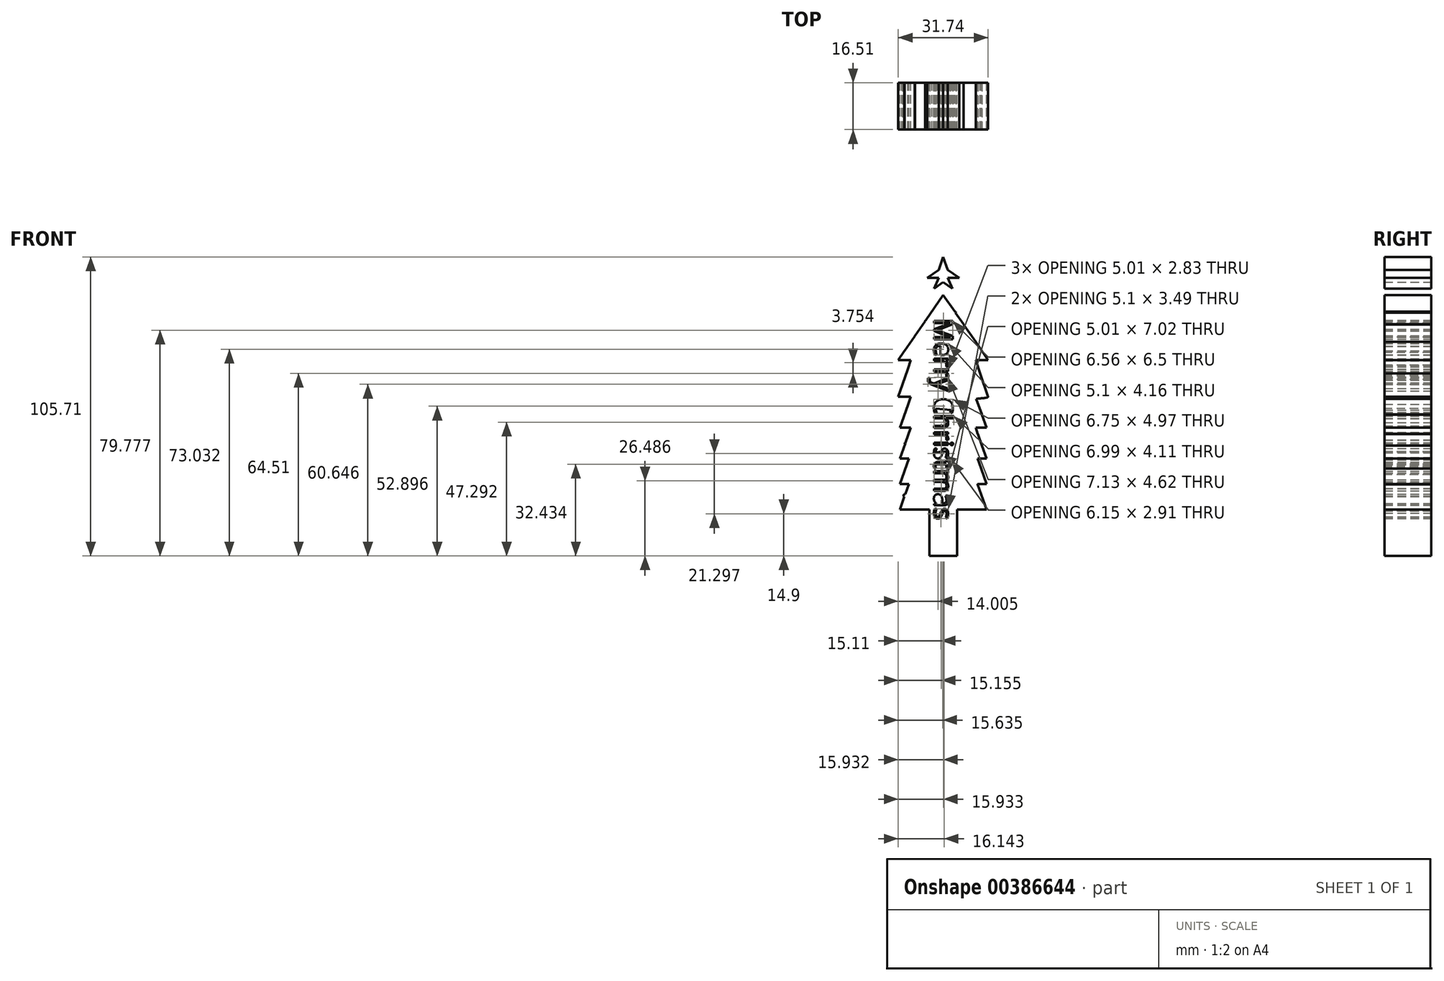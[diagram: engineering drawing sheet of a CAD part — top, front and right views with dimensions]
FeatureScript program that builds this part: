
annotation { "Feature Type Name" : "Feature", "Feature Type Description" : "" }
export const myFeature = defineFeature(function(context is Context, id is Id, definition is map)
    precondition{}
    {
        {
            var Q0;
            Q0=qCreatedBy(makeId("Front.planeOp"),FACE);
            var sketch = newSketch(context, id + "F0", { "sketchPlane" : qUnion([Q0])});
            skLineSegment(sketch, "E0", {"start": v(0, -45.28) * mm, "end": v(-4.85, -45.28) * mm});
            skLineSegment(sketch, "E1", {"start": v(-4.85, -45.28) * mm, "end": v(-4.85, -28.85) * mm});
            skLineSegment(sketch, "E2", {"start": v(-4.85, -28.85) * mm, "end": v(-15.31, -28.85) * mm});
            skLineSegment(sketch, "E3", {"start": v(-15.31, -28.85) * mm, "end": v(-12.14, -19.89) * mm});
            skLineSegment(sketch, "E4", {"start": v(-12.14, -19.89) * mm, "end": v(-15.31, -19.89) * mm});
            skLineSegment(sketch, "E5", {"start": v(-15.31, -19.89) * mm, "end": v(-12.14, -10.92) * mm});
            skLineSegment(sketch, "E6", {"start": v(-12.14, -10.92) * mm, "end": v(-15.31, -10.92) * mm});
            skLineSegment(sketch, "E7", {"start": v(-15.31, -10.92) * mm, "end": v(-11.44, 0) * mm});
            skLineSegment(sketch, "E8", {"start": v(-11.44, 0) * mm, "end": v(-15.31, 0) * mm});
            skLineSegment(sketch, "E9", {"start": v(-15.31, 0) * mm, "end": v(-11.44, 10.92) * mm});
            skLineSegment(sketch, "E10", {"start": v(-11.44, 10.92) * mm, "end": v(-15.87, 10.92) * mm});
            skLineSegment(sketch, "E11", {"start": v(-15.87, 10.92) * mm, "end": v(-11.44, 24) * mm});
            skLineSegment(sketch, "E12", {"start": v(-11.44, 24) * mm, "end": v(-15.87, 24) * mm});
            skLineSegment(sketch, "E13", {"start": v(-15.87, 24) * mm, "end": v(0, 46.96) * mm});
            skLineSegment(sketch, "E14", {"start": v(0, 46.96) * mm, "end": v(0, -45.28) * mm, "construction": true});
            skLineSegment(sketch, "E15.MirrorCS", {"start": v(15.87, 24) * mm, "end": v(0, 46.96) * mm});
            skLineSegment(sketch, "E16.MirrorCS", {"start": v(15.87, 10.92) * mm, "end": v(11.44, 24) * mm});
            skLineSegment(sketch, "E17.MirrorCS", {"start": v(11.44, 24) * mm, "end": v(15.87, 24) * mm});
            skLineSegment(sketch, "E18.MirrorCS", {"start": v(11.44, 10.92) * mm, "end": v(15.87, 10.92) * mm});
            skLineSegment(sketch, "E19.MirrorCS", {"start": v(15.31, 0) * mm, "end": v(11.44, 10.92) * mm});
            skLineSegment(sketch, "E20.MirrorCS", {"start": v(11.44, 0) * mm, "end": v(15.31, 0) * mm});
            skLineSegment(sketch, "E21.MirrorCS", {"start": v(15.31, -10.92) * mm, "end": v(11.44, 0) * mm});
            skLineSegment(sketch, "E22.MirrorCS", {"start": v(12.14, -10.92) * mm, "end": v(15.31, -10.92) * mm});
            skLineSegment(sketch, "E23.MirrorCS", {"start": v(15.31, -19.89) * mm, "end": v(12.14, -10.92) * mm});
            skLineSegment(sketch, "E24.MirrorCS", {"start": v(12.14, -19.89) * mm, "end": v(15.31, -19.89) * mm});
            skLineSegment(sketch, "E25.MirrorCS", {"start": v(15.31, -28.85) * mm, "end": v(12.14, -19.89) * mm});
            skLineSegment(sketch, "E26.MirrorCS", {"start": v(4.85, -28.85) * mm, "end": v(15.31, -28.85) * mm});
            skLineSegment(sketch, "E27.MirrorCS", {"start": v(4.85, -45.28) * mm, "end": v(4.85, -28.85) * mm});
            skLineSegment(sketch, "E28.MirrorCS", {"start": v(0, -45.28) * mm, "end": v(4.85, -45.28) * mm});
            skLineSegment(sketch, "E29", {"start": v(0, 51.48) * mm, "end": v(0, 46.96) * mm});
            skLineSegment(sketch, "E30", {"start": v(0, 51.48) * mm, "end": v(-3.26, 49.22) * mm});
            skPoint(sketch, "E30.endSnap0", {"position": v(0, 49.22) * mm});
            skLineSegment(sketch, "E31", {"start": v(-3.26, 49.22) * mm, "end": v(-1.63, 53.05) * mm});
            skPoint(sketch, "E31.endSnap0", {"position": v(-1.63, 50.35) * mm});
            skLineSegment(sketch, "E32", {"start": v(-1.63, 53.05) * mm, "end": v(-5.67, 53.05) * mm});
            skLineSegment(sketch, "E33", {"start": v(-5.67, 53.05) * mm, "end": v(-1.63, 55.84) * mm});
            skLineSegment(sketch, "E34", {"start": v(-1.63, 55.84) * mm, "end": v(0, 60.43) * mm});
            skLineSegment(sketch, "E35", {"start": v(0, 60.43) * mm, "end": v(0, 51.48) * mm});
            skLineSegment(sketch, "E36.MirrorCS", {"start": v(1.63, 55.84) * mm, "end": v(0, 60.43) * mm});
            skLineSegment(sketch, "E37.MirrorCS", {"start": v(5.67, 53.05) * mm, "end": v(1.63, 55.84) * mm});
            skLineSegment(sketch, "E38.MirrorCS", {"start": v(1.63, 53.05) * mm, "end": v(5.67, 53.05) * mm});
            skLineSegment(sketch, "E39.MirrorCS", {"start": v(0, 51.48) * mm, "end": v(3.26, 49.22) * mm});
            skLineSegment(sketch, "E40.MirrorCS", {"start": v(3.26, 49.22) * mm, "end": v(1.63, 53.05) * mm});
            skPoint(sketch, "E41.13.internal.snap0", {"position": v(13.66, 10.92) * mm});
            skPoint(sketch, "E41.16.internal.snap0", {"position": v(-13.38, -5.46) * mm});
            skPoint(sketch, "E41.16.internal.snap1", {"position": v(-13.66, 17.46) * mm});
            skPoint(sketch, "E41.17.internal.snap0", {"position": v(13.66, 10.92) * mm});
            skPoint(sketch, "E41.19.internal.snap0", {"position": v(13.38, 5.46) * mm});
            skPoint(sketch, "E41.22.internal.snap0", {"position": v(-13.38, -5.46) * mm});
            skFitSpline(sketch, "E41", {"points": [v(-4.38, 40.63) * mm, v(4.29, 40.76) * mm, v(-6.42, 37.67) * mm, v(7.18, 36.57) * mm, v(-10.08, 32.37) * mm, v(11.47, 30.36) * mm, v(-13.73, 27.1) * mm, v(11.44, 24) * mm, v(-12.53, 20.79) * mm, v(13.05, 19.25) * mm, v(-14.4, 15.25) * mm, v(15.87, 10.92) * mm, v(-12.37, 8.3) * mm, v(13.66, 4.67) * mm, v(-14.67, 1.82) * mm, v(12.22, -2.2) * mm, v(-13.66, -5.46) * mm, v(13.66, -6.25) * mm, v(-12.14, -10.92) * mm, v(13.38, -14.42) * mm, v(-14.36, -17.19) * mm, v(12.14, -19.89) * mm, v(-13.38, -23.39) * mm, v(15.31, -28.85) * mm], "startDerivative": vector(572.28, 38.3) * mm, "endDerivative": vector(1029.2, -121.9) * mm});
            skText(sketch, "E42", { "text": "Merry Christmas", "fontName": "OpenSans-Regular.ttf"});
            const initialGuessF0  = {"E42": [-0.00322, 0.03865, 0, -1, 0.00662]};
            skSetInitialGuess(sketch, initialGuessF0);
            skSolve(sketch);
        }
        {
            var Q0;
            Q0 = qSketchRegion(id + "F0", true);
            extrude(context, id + "F1", {"entities" : qUnion([Q0]), "depth" : 16.5 * mm});
        }
    });
